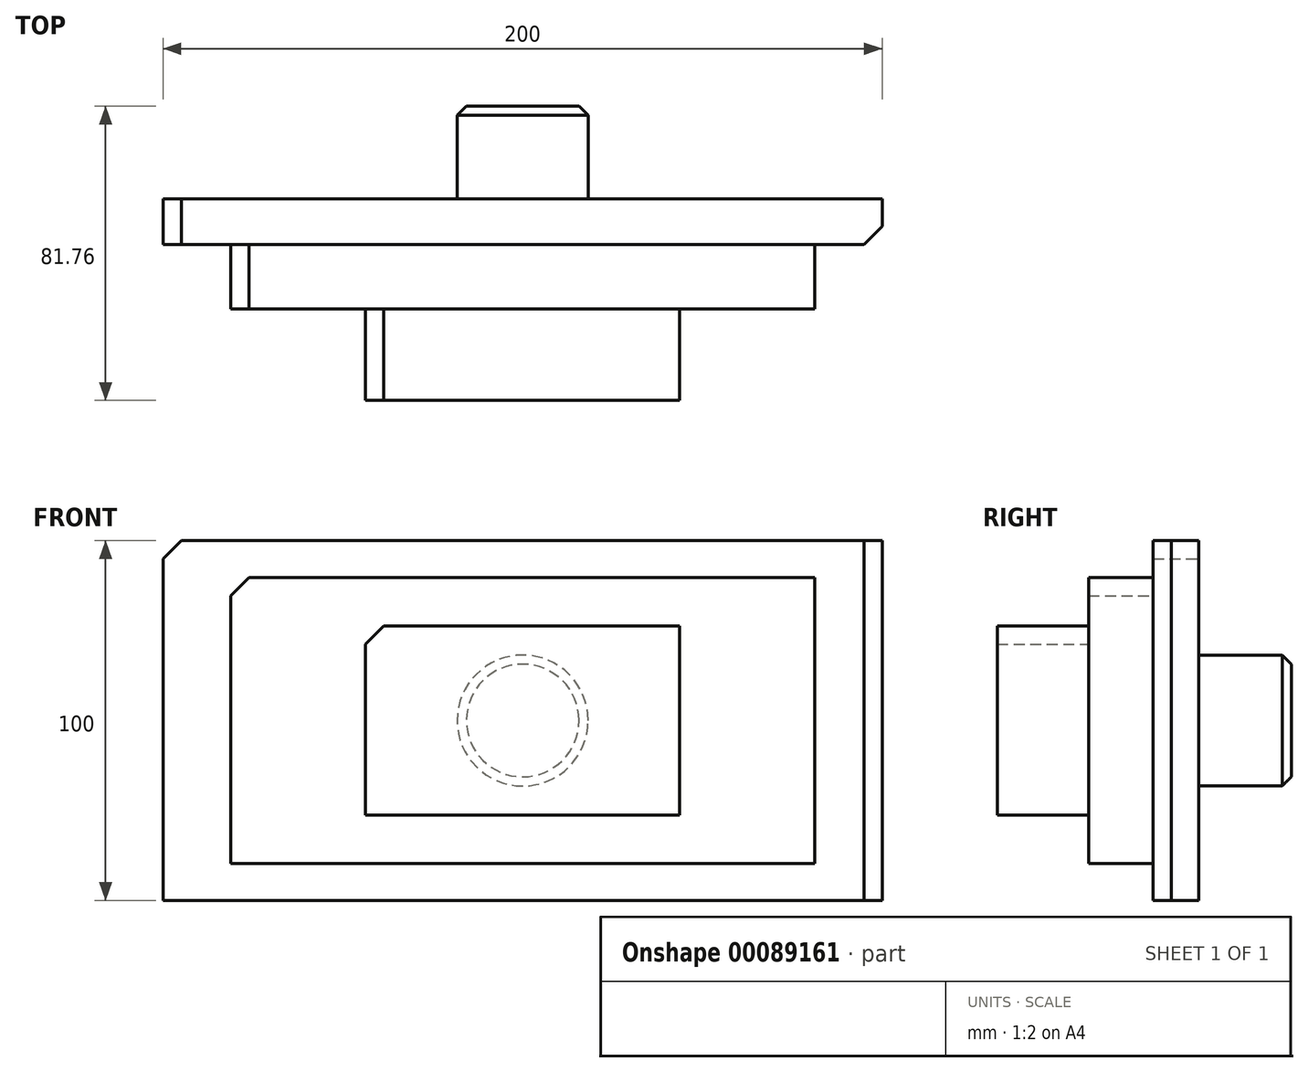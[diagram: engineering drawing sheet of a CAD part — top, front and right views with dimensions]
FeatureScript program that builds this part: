
annotation { "Feature Type Name" : "Feature", "Feature Type Description" : "" }
export const myFeature = defineFeature(function(context is Context, id is Id, definition is map)
    precondition{}
    {
        {
            var Q0;
            Q0=qCreatedBy(makeId("Front.planeOp"),FACE);
            var sketch = newSketch(context, id + "F0", { "sketchPlane" : qUnion([Q0])});
            skLineSegment(sketch, "E0.bottom", {"start": v(100, 50) * mm, "end": v(-100, 50) * mm});
            skLineSegment(sketch, "E0.top", {"start": v(100, -50) * mm, "end": v(-100, -50) * mm});
            skLineSegment(sketch, "E0.left", {"start": v(100, 50) * mm, "end": v(100, -50) * mm});
            skLineSegment(sketch, "E0.right", {"start": v(-100, 50) * mm, "end": v(-100, -50) * mm});
            skPoint(sketch, "E0.middle", {"position": v(0, 0) * mm});
            skLineSegment(sketch, "E1.bottom", {"start": v(81.2, 39.76) * mm, "end": v(-81.2, 39.76) * mm});
            skLineSegment(sketch, "E1.top", {"start": v(81.2, -39.76) * mm, "end": v(-81.2, -39.76) * mm});
            skLineSegment(sketch, "E1.left", {"start": v(81.2, 39.76) * mm, "end": v(81.2, -39.76) * mm});
            skLineSegment(sketch, "E1.right", {"start": v(-81.2, 39.76) * mm, "end": v(-81.2, -39.76) * mm});
            skSolve(sketch);
        }
        {
            var Q0;
            Q0 = qSketchRegion(id + "F0", true);
            extrude(context, id + "F1", {"entities" : qUnion([Q0]), "depth" : 12.7 * mm});
        }
        {
            var Q0;
            Q0=makeQuery(id+"F0.imprint","IMPRINT",FACE,{"disambiguationData":[TD([[makeQuery(id+"F0.imprint","IMPRINT",EDGE,{"derivedFrom":sQuery(id+"F0.wireOp",EDGE,"E1.bottom")}),1.0]])]});
            extrude(context, id + "F2", {"entities" : qUnion([Q0]), "operationType" : NewBodyOperationType.ADD, "depth" : 30.65 * mm});
        }
        {
            var Q0;
            Q0=makeQuery(id+"F2.opExtrude","CAP_FACE",FACE,{"disambiguationData":[OSD([sQuery(id+"F0.wireOp",EDGE,"E1.bottom"),sQuery(id+"F0.wireOp",EDGE,"E1.top"),sQuery(id+"F0.wireOp",EDGE,"E1.left"),sQuery(id+"F0.wireOp",EDGE,"E1.right")])],"isStart":false});
            var sketch = newSketch(context, id + "F3", { "sketchPlane" : qUnion([Q0])});
            skCircle(sketch, "E2", {"center": v(0, 0) * mm, "radius": 18.2 * mm});
            skSolve(sketch);
        }
        {
            var Q0;
            Q0 = qSketchRegion(id + "F3", true);
            extrude(context, id + "F4", {"entities" : qUnion([Q0]), "operationType" : NewBodyOperationType.REMOVE, "oppositeDirection" : true, "depth" : 77.93 * mm});
        }
        {
            var Q0;
            Q0=makeQuery(id+"F2.opExtrude","CAP_FACE",FACE,{"disambiguationData":[OSD([sQuery(id+"F0.wireOp",EDGE,"E1.bottom"),sQuery(id+"F0.wireOp",EDGE,"E1.top"),sQuery(id+"F0.wireOp",EDGE,"E1.left"),sQuery(id+"F0.wireOp",EDGE,"E1.right")])],"isStart":false});
            var sketch = newSketch(context, id + "F5", { "sketchPlane" : qUnion([Q0])});
            skLineSegment(sketch, "E3.bottom", {"start": v(43.69, 26.24) * mm, "end": v(-43.69, 26.24) * mm});
            skLineSegment(sketch, "E3.top", {"start": v(43.69, -26.24) * mm, "end": v(-43.69, -26.24) * mm});
            skLineSegment(sketch, "E3.left", {"start": v(43.69, 26.24) * mm, "end": v(43.69, -26.24) * mm});
            skLineSegment(sketch, "E3.right", {"start": v(-43.69, 26.24) * mm, "end": v(-43.69, -26.24) * mm});
            skPoint(sketch, "E3.middle", {"position": v(0, 0) * mm});
            skSolve(sketch);
        }
        {
            var Q0;
            Q0 = qSketchRegion(id + "F5", true);
            extrude(context, id + "F6", {"entities" : qUnion([Q0]), "depth" : 25.4 * mm});
        }
        {
            var Q0;
            Q0=makeQuery(id+"F0.imprint","IMPRINT",FACE,{"disambiguationData":[TD([[makeQuery(id+"F0.imprint","IMPRINT",EDGE,{"derivedFrom":sQuery(id+"F0.wireOp",EDGE,"E1.bottom")}),1.0]])]});
            var sketch = newSketch(context, id + "F7", { "sketchPlane" : qUnion([Q0])});
            skCircle(sketch, "E4.0", {"center": v(0, 0) * mm, "radius": 18.2 * mm});
            skSolve(sketch);
        }
        {
            var Q0;
            Q0 = qSketchRegion(id + "F7", true);
            extrude(context, id + "F8", {"entities" : qUnion([Q0]), "operationType" : NewBodyOperationType.ADD, "oppositeDirection" : true, "depth" : 25.71 * mm});
        }
        {
            var Q0;
            Q0=makeQuery(id+"F8.opExtrude","CAP_FACE",FACE,{"disambiguationData":[OSD([sQuery(id+"F7.wireOp",EDGE,"E4.0")])],"isStart":true});
            var sketch = newSketch(context, id + "F9", { "sketchPlane" : qUnion([Q0])});
            skCircle(sketch, "E5.0", {"center": v(0, 0) * mm, "radius": 18.2 * mm});
            skSolve(sketch);
        }
        {
            var Q0;
            Q0 = qSketchRegion(id + "F9", true);
            extrude(context, id + "F10", {"entities" : qUnion([Q0]), "operationType" : NewBodyOperationType.ADD, "depth" : 33.75 * mm});
        }
        {
            var Q0;
            Q0=makeQuery(id+"F6.opExtrude","SWEPT_EDGE",EDGE,{"disambiguationData":[OSD([sQuery(id+"F5.wireOp",EDGE,"E3.bottom"),sQuery(id+"F5.wireOp",EDGE,"E3.right")])]});
            var Q1;
            Q1=makeQuery(id+"F1.opExtrude","CAP_EDGE",EDGE,{"disambiguationData":[OSD([sQuery(id+"F0.wireOp",EDGE,"E0.left")])],"isStart":false});
            var Q2;
            Q2=makeQuery(id+"F2.opExtrude","SWEPT_EDGE",EDGE,{"disambiguationData":[OSD([sQuery(id+"F0.wireOp",EDGE,"E1.bottom"),sQuery(id+"F0.wireOp",EDGE,"E1.right")])]});
            var Q3;
            Q3=makeQuery(id+"F1.opExtrude","SWEPT_EDGE",EDGE,{"disambiguationData":[OSD([sQuery(id+"F0.wireOp",EDGE,"E0.bottom"),sQuery(id+"F0.wireOp",EDGE,"E0.right")])]});
            chamfer(context, id + "F11", {"entities" : qUnion([Q0, Q1, Q2, Q3]), "width" : 5.08 * mm, "tangentPropagation" : true});
        }
        {
            var Q0;
            Q0=makeQuery(id+"F8.opExtrude","CAP_EDGE",EDGE,{"disambiguationData":[OSD([sQuery(id+"F7.wireOp",EDGE,"E4.0")])],"isStart":false});
            chamfer(context, id + "F12", {"entities" : qUnion([Q0]), "width" : 2.54 * mm});
        }
    });
